# Revit family: door_nanawall_cero_ii_unit_a
name_source: partatom
category: Doors
revit_build: Autodesk Revit 2018 (Build: 20170223_1515(x64)
units: mm (PartAtom-declared; Revit-internal decimal feet)

## family parameters
Always vertical = Yes
Cut with Voids When Loaded = No
Host = Wall
OmniClass Number = 23.30.10.17.11
OmniClass Title = Sliding Doors
Room Calculation Point = Yes
Shared = No

## types (8) — shared parameters
Actual Height = 7' - 0"
Actual Panel Width = 2' - 6"
Actual Width = 5' - 6 157/256"
Analytic Construction = Metal frame, double/triple glass, glass storm
C to C = 0' - 3 99/256"
C to Ext = 0' - 1 51/128"
C to Int = 0' - 4 201/256"
Construction Type = New Construction
Elevation D = No
Finish = Metal - Nanawall - Clear (anodized)
Function = Exterior
Glass Lite Thickness = 0' - 0 1/4"
Glazing Material = Glass - NanaWall - Generic
Glazing Thickness = 0' - 1 107/256"
Half Thickness = 0' - 0 3/8"
Heat Transfer Coefficient (U) = 0.49 BTU/(h·ft²·°F)
Height = 7' - 0"
Height C = 7' - 0"
Inset Note = To set Door into wall use Inset parameter found in Instance Properties.
Installation and Service URL = https://www.nanawall.com
Manufacturer = NanaWall
Manufacturer Fax Number = (415) 383-0312
Model = Cero II - Unit A
Operation = Sliding
Panel Width = 2' - 6"
Panel Width C = 2' - 6"
Performance URL = https://www.nanawall.com
Product Name = Cero
Product Page URL = https://www.nanawall.com
Rough Height = 7' - 0 1/2"
Rough Offset = 0' - 0 1/2"
Rough Width = 5' - 7 157/256"
S Glazing = 0' - 3 25/32"
Size Note = Contact Nanawall for Larger Sizes
Sizing Statement = Maximum Panel Size = 7' 4 1/2 (W) x 13' 1 (H) (2250 mm x 4000 mm)
Subcategory = Sliding Glass Wall
Thermal Resistance (R) = 2.0409 (h·ft²·°F)/BTU
Thickness = 0' - 0 3/4"
Top Glazing = 0' - 3 25/32"
URL = https://www.nanawall.com
Version = 2014-v1.0a
Wall Closure = By host
Warranty URL = https://www.nanawall.com
Width = 5' - 6 157/256"
Width C = 5' - 6 157/256"
zero-valued in all types: Solar Heat Gain Coefficient, Visual Light Transmittance

## per-type parameters (varying)
| type | Bottom Glazing | Bottom Sash | Description | Flush Saddle Hybrid Sill | Flush Sill | Higher Weather Performance Sill | Low Profile Saddle Sill | Lower Sills | Panel Height | Sill Height | XO | XO Sill Filler C | XX |
| Cero_II-XO_Configuration with Higher Weather Performance Sill | 0' - 3 25/32" | 0' - 2 31/128" | Sliding Glass Wall - XO Configuration | No | No | Yes | No | No | 6' - 7 33/64" | 0' - 2 61/64" | Yes | Yes | No |
| Cero_II-XX_Configuration with Higher Weather Performance Sill | 0' - 3 25/32" | 0' - 2 31/128" | Sliding Glass Wall - XX Configuration | No | No | Yes | No | No | 6' - 7 33/64" | 0' - 2 61/64" | No | No | Yes |
| Cero_II-XO_Configuration with Flush Sill | 0' - 1 103/128" | 0' - 0 49/256" | Sliding Glass Wall - XO Configuration | No | Yes | No | No | Yes | 6' - 9 145/256" | 0' - 0" | Yes | No | No |
| Cero_II-XO_Configuration with Flush Saddle Hybrid Sill | 0' - 2 71/256" | 0' - 0 95/128" | Sliding Glass Wall - XO Configuration | Yes | No | No | No | Yes | 6' - 9 1/64" | 0' - 0 141/256" | Yes | No | No |
| Cero_II-XO_Configuration with Low Profile Saddle Sill | 0' - 2 71/256" | 0' - 0 95/128" | Sliding Glass Wall - XO Configuration | No | No | No | Yes | Yes | 6' - 9 1/64" | 0' - 0 141/256" | Yes | No | No |
| Cero_II-XX_Configuration with Flush Sill | 0' - 1 103/128" | 0' - 0 49/256" | Sliding Glass Wall - XX Configuration | No | Yes | No | No | Yes | 6' - 9 145/256" | 0' - 0" | No | No | Yes |
| Cero_II-XX_Configuration with Flush Saddle Hybrid Sill | 0' - 2 71/256" | 0' - 0 95/128" | Sliding Glass Wall - XX Configuration | Yes | No | No | No | Yes | 6' - 9 1/64" | 0' - 0 141/256" | No | No | Yes |
| Cero_II-XX_Configuration with Low Profile Saddle Sill | 0' - 2 71/256" | 0' - 0 95/128" | Sliding Glass Wall - XX Configuration | No | No | No | Yes | Yes | 6' - 9 1/64" | 0' - 0 141/256" | No | No | Yes |

## geometry (parser evidence)
native form markers: Blend x874, Sweep x22
no freeform markers — native parametric forms only
